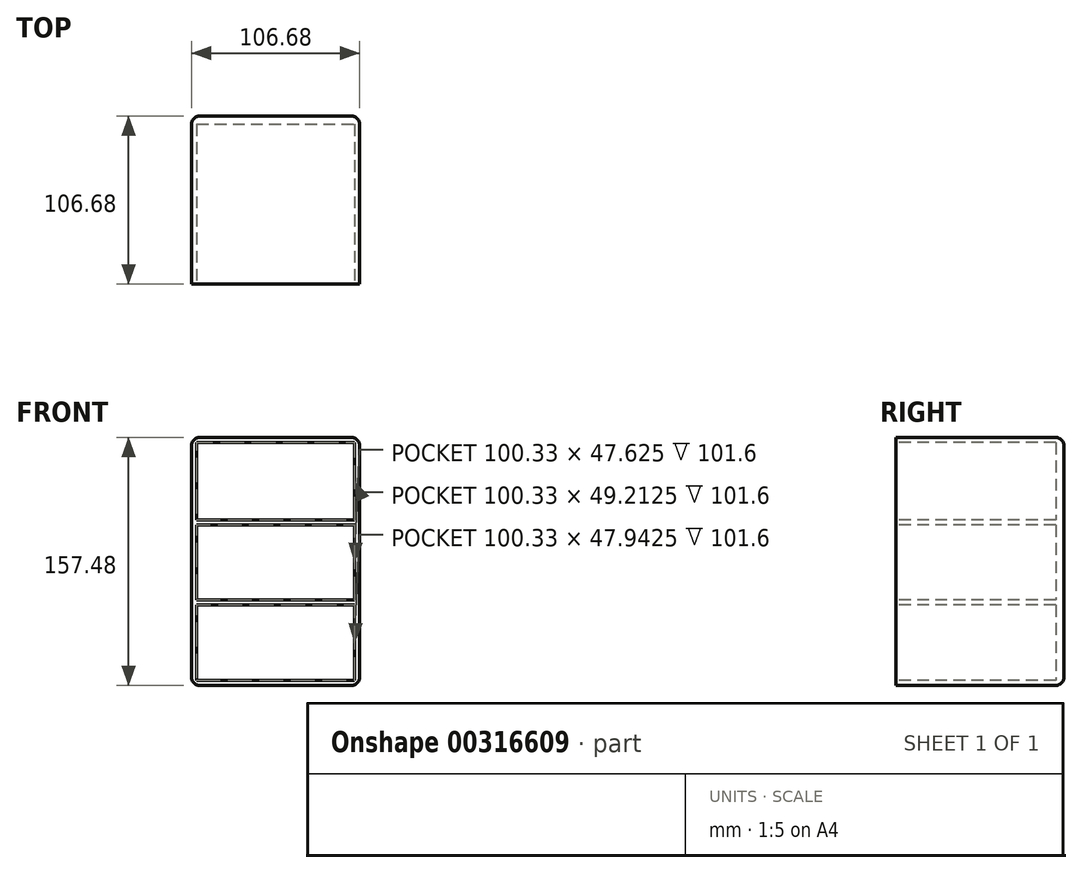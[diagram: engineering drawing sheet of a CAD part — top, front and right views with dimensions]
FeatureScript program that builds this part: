
annotation { "Feature Type Name" : "Feature", "Feature Type Description" : "" }
export const myFeature = defineFeature(function(context is Context, id is Id, definition is map)
    precondition{}
    {
        {
            var Q0;
            Q0=qCreatedBy(makeId("Front.planeOp"),FACE);
            var sketch = newSketch(context, id + "F0", { "sketchPlane" : qUnion([Q0])});
            skLineSegment(sketch, "E0.bottom", {"start": v(-51.12, 110.97) * mm, "end": v(55.56, 110.97) * mm});
            skLineSegment(sketch, "E0.top", {"start": v(-51.12, -46.51) * mm, "end": v(55.56, -46.51) * mm});
            skLineSegment(sketch, "E0.left", {"start": v(-51.12, 110.97) * mm, "end": v(-51.12, -46.51) * mm});
            skLineSegment(sketch, "E0.right", {"start": v(55.56, 110.97) * mm, "end": v(55.56, -46.51) * mm});
            skSolve(sketch);
        }
        {
            var Q0;
            Q0=qSketchRegion(id+"F0",true);
            extrude(context, id + "F1", {"entities" : qUnion([Q0]), "depth" : 106.68 * mm});
        }
        {
            var Q0;
            Q0=makeQuery(id+"F1.opExtrude","CAP_FACE",FACE,{"disambiguationData":[OSD([sQuery(id+"F0.wireOp",EDGE,"E0.bottom"),sQuery(id+"F0.wireOp",EDGE,"E0.top"),sQuery(id+"F0.wireOp",EDGE,"E0.left"),sQuery(id+"F0.wireOp",EDGE,"E0.right")])],"isStart":false});
            var sketch = newSketch(context, id + "F2", { "sketchPlane" : qUnion([Q0])});
            skLineSegment(sketch, "E1.bottom", {"start": v(-47.94, 107.8) * mm, "end": v(52.39, 107.8) * mm});
            skLineSegment(sketch, "E1.top", {"start": v(-47.94, -43.34) * mm, "end": v(52.39, -43.34) * mm});
            skLineSegment(sketch, "E1.left", {"start": v(-47.94, 107.8) * mm, "end": v(-47.94, -43.34) * mm});
            skLineSegment(sketch, "E1.right", {"start": v(52.39, 107.8) * mm, "end": v(52.39, -43.34) * mm});
            skSolve(sketch);
        }
        {
            var Q0;
            Q0=qSketchRegion(id+"F2",true);
            extrude(context, id + "F3", {"entities" : qUnion([Q0]), "operationType" : NewBodyOperationType.REMOVE, "oppositeDirection" : true, "depth" : 101.6 * mm});
        }
        {
            var Q0;
            Q0=makeQuery(id+"F1.opExtrude","CAP_FACE",FACE,{"disambiguationData":[OSD([sQuery(id+"F0.wireOp",EDGE,"E0.bottom"),sQuery(id+"F0.wireOp",EDGE,"E0.top"),sQuery(id+"F0.wireOp",EDGE,"E0.left"),sQuery(id+"F0.wireOp",EDGE,"E0.right")])],"isStart":false});
            var sketch = newSketch(context, id + "F4", { "sketchPlane" : qUnion([Q0])});
            skLineSegment(sketch, "E2.bottom", {"start": v(-51.12, 55.4) * mm, "end": v(55.56, 55.4) * mm});
            skLineSegment(sketch, "E2.top", {"start": v(-51.12, 58.58) * mm, "end": v(55.56, 58.58) * mm});
            skLineSegment(sketch, "E2.left", {"start": v(-51.12, 58.58) * mm, "end": v(-51.12, 55.4) * mm});
            skLineSegment(sketch, "E2.right", {"start": v(55.56, 58.58) * mm, "end": v(55.56, 55.4) * mm});
            skLineSegment(sketch, "E3.bottom", {"start": v(-51.12, 7.78) * mm, "end": v(55.56, 7.78) * mm});
            skLineSegment(sketch, "E3.top", {"start": v(-51.12, 4.6) * mm, "end": v(55.56, 4.6) * mm});
            skLineSegment(sketch, "E3.left", {"start": v(-51.12, 7.78) * mm, "end": v(-51.12, 4.6) * mm});
            skLineSegment(sketch, "E3.right", {"start": v(55.56, 7.78) * mm, "end": v(55.56, 4.6) * mm});
            skLineSegment(sketch, "E4", {"start": v(55.56, 6.2) * mm, "end": v(-51.12, 6.2) * mm});
            skLineSegment(sketch, "E5", {"start": v(-51.12, 57) * mm, "end": v(55.56, 57) * mm});
            skSolve(sketch);
        }
        {
            var Q0;
            Q0=qSketchRegion(id+"F4",true);
            extrude(context, id + "F5", {"entities" : qUnion([Q0]), "operationType" : NewBodyOperationType.ADD, "oppositeDirection" : true, "depth" : 101.6 * mm});
        }
        {
            var Q0;
            Q0=makeQuery(id+"F1.opExtrude","SWEPT_EDGE",EDGE,{"disambiguationData":[OSD([sQuery(id+"F0.wireOp",EDGE,"E0.bottom"),sQuery(id+"F0.wireOp",EDGE,"E0.right")])]});
            var Q1;
            Q1=makeQuery(id+"F1.opExtrude","SWEPT_EDGE",EDGE,{"disambiguationData":[OSD([sQuery(id+"F0.wireOp",EDGE,"E0.bottom"),sQuery(id+"F0.wireOp",EDGE,"E0.left")])]});
            var Q2;
            Q2=makeQuery(id+"F1.opExtrude","SWEPT_EDGE",EDGE,{"disambiguationData":[OSD([sQuery(id+"F0.wireOp",EDGE,"E0.top"),sQuery(id+"F0.wireOp",EDGE,"E0.right")])]});
            var Q3;
            Q3=makeQuery(id+"F1.opExtrude","SWEPT_EDGE",EDGE,{"disambiguationData":[OSD([sQuery(id+"F0.wireOp",EDGE,"E0.top"),sQuery(id+"F0.wireOp",EDGE,"E0.left")])]});
            var Q4;
            Q4=makeQuery(id+"F1.opExtrude","CAP_EDGE",EDGE,{"disambiguationData":[OSD([sQuery(id+"F0.wireOp",EDGE,"E0.left")])],"isStart":true});
            var Q5;
            Q5=makeQuery(id+"F1.opExtrude","CAP_EDGE",EDGE,{"disambiguationData":[OSD([sQuery(id+"F0.wireOp",EDGE,"E0.bottom")])],"isStart":true});
            var Q6;
            Q6=makeQuery(id+"F1.opExtrude","CAP_EDGE",EDGE,{"disambiguationData":[OSD([sQuery(id+"F0.wireOp",EDGE,"E0.right")])],"isStart":true});
            var Q7;
            Q7=makeQuery(id+"F1.opExtrude","CAP_EDGE",EDGE,{"disambiguationData":[OSD([sQuery(id+"F0.wireOp",EDGE,"E0.top")])],"isStart":true});
            fillet(context, id + "F6", {"entities" : qUnion([Q0, Q1, Q2, Q3, Q4, Q5, Q6, Q7]), "radius" : 5.08 * mm, "tangentPropagation" : true, "allowEdgeOverflow" : false});
        }
    });
